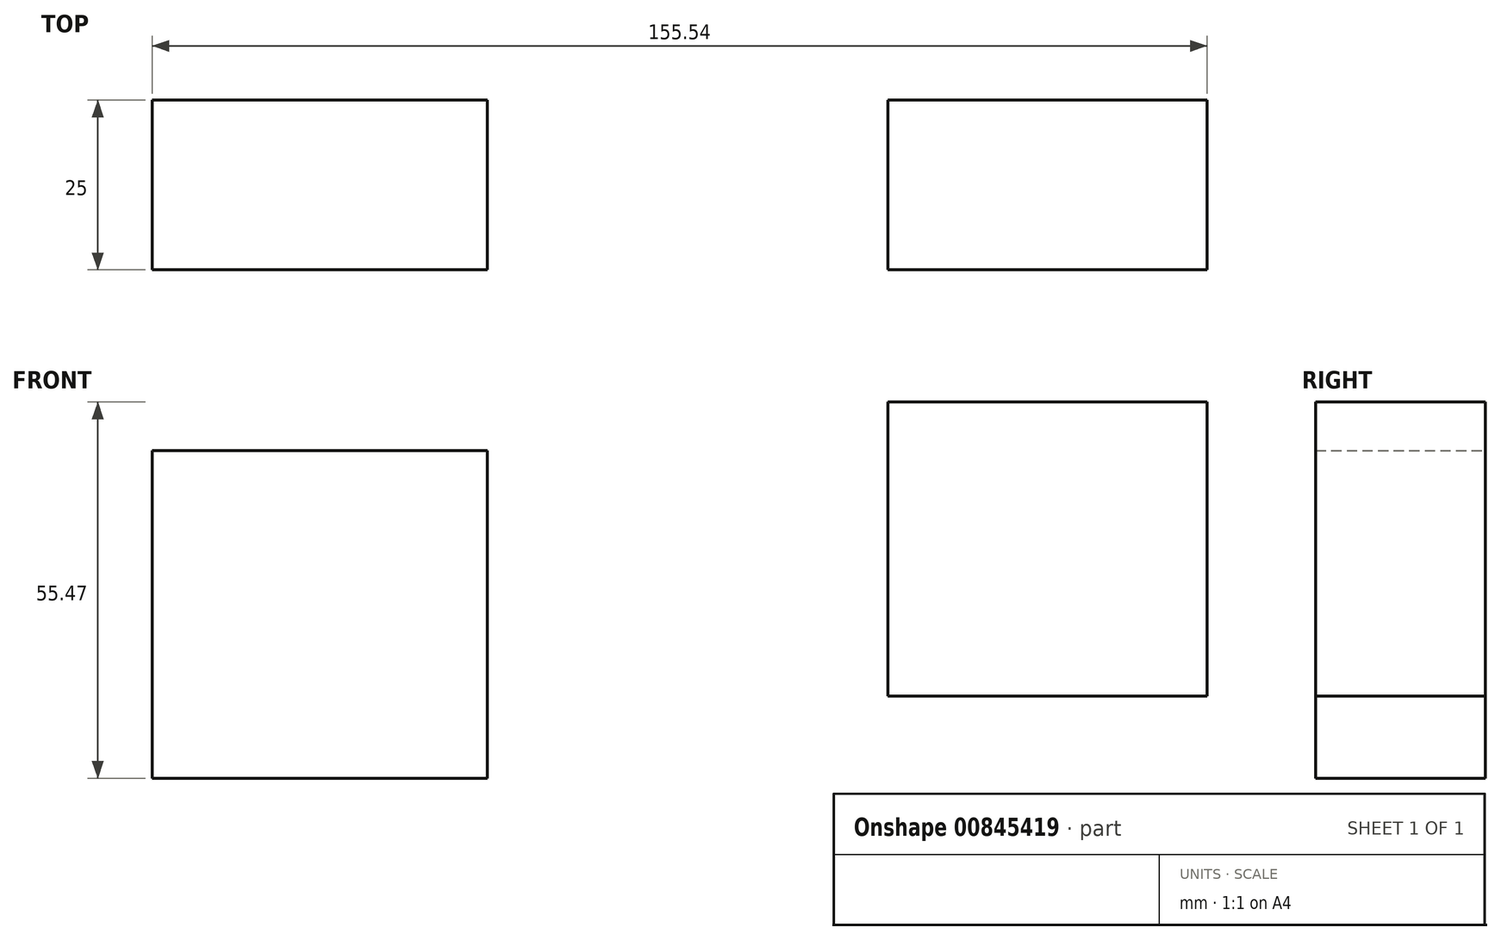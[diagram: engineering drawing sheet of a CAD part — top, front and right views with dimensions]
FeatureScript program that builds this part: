
annotation { "Feature Type Name" : "Feature", "Feature Type Description" : "" }
export const myFeature = defineFeature(function(context is Context, id is Id, definition is map)
    precondition{}
    {
        {
            var Q0;
            Q0=qCreatedBy(makeId("Front.planeOp"),FACE);
            var sketch = newSketch(context, id + "F0", { "sketchPlane" : qUnion([Q0])});
            skLineSegment(sketch, "E0.bottom", {"start": v(-108.48, 48.3) * mm, "end": v(-59.08, 48.3) * mm});
            skLineSegment(sketch, "E0.top", {"start": v(-108.48, 0) * mm, "end": v(-59.08, 0) * mm});
            skLineSegment(sketch, "E0.left", {"start": v(-108.48, 48.3) * mm, "end": v(-108.48, 0) * mm});
            skLineSegment(sketch, "E0.right", {"start": v(-59.08, 48.3) * mm, "end": v(-59.08, 0) * mm});
            skLineSegment(sketch, "E1.bottom", {"start": v(0, 55.47) * mm, "end": v(47.06, 55.47) * mm});
            skLineSegment(sketch, "E1.top", {"start": v(0, 12.08) * mm, "end": v(47.06, 12.08) * mm});
            skLineSegment(sketch, "E1.left", {"start": v(0, 55.47) * mm, "end": v(0, 12.08) * mm});
            skLineSegment(sketch, "E1.right", {"start": v(47.06, 55.47) * mm, "end": v(47.06, 12.08) * mm});
            skSolve(sketch);
        }
        {
            var Q0;
            Q0=makeQuery(id+"F0.imprint","IMPRINT",FACE,{"disambiguationData":[TD([[makeQuery(id+"F0.imprint","IMPRINT",EDGE,{"derivedFrom":sQuery(id+"F0.wireOp",EDGE,"E0.bottom")}),-1.0]])]});
            var Q1;
            Q1=makeQuery(id+"F0.imprint","IMPRINT",FACE,{"disambiguationData":[TD([[makeQuery(id+"F0.imprint","IMPRINT",EDGE,{"derivedFrom":sQuery(id+"F0.wireOp",EDGE,"E1.bottom")}),-1.0]])]});
            extrude(context, id + "F1", {"entities" : qUnion([Q0, Q1]), "depth" : 25 * mm, "offsetDistance" : 25 * mm});
        }
    });
